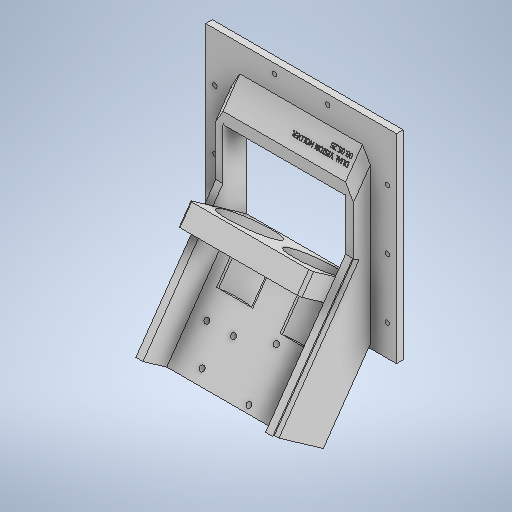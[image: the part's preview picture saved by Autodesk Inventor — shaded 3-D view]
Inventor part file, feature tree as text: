
AUTODESK INVENTOR PART (.ipt)
format: ipt  version: 2025.2 (Build 292293000, 293)  size: 1,523,200 bytes
history: native  units: in
note: dims shown in document units (in); Inventor stores cm internally (conversion verified against a paired STEP export)
features: sketch x51, extrude x46, projected_geometry x8, plane x5, chamfer x2, move_body x1, fillet x1, hole x1
ambient origin geometry x8: Origin, YZ Plane, XZ Plane, XY Plane, X Axis, Y Axis, Z Axis, Center Point
bodies: Solid1 (feature_tree)
feature tree (115):
  extrude  "Extrusion1"  Depth=0.1969in TaperAngle=0.0deg
  move_body  "Move Body1"
  plane  "Work Plane1"
  sketch  "Sketch5"  dims[d5=1.7717in d6=1.7717in d7=1.7717in d8=1.7717in d9=0.8108in d10=90.0deg d11=0.0787in d12=0.3701in d13=0.4252in d14=0.1362in d15=-0.0984in d16=-0.0591in d17=0.0in]
  plane  "Work Plane2"
  extrude  "Extrusion4"  TaperAngle=0.0deg  [1 undecoded]
  extrude  "Extrusion6"  Depth=0.2405in
  extrude  "Extrusion8"  Depth=2.5591in TaperAngle=0.0deg
  chamfer  "Chamfer1"  [1 undecoded]
  extrude  "Extrusion11"  Depth=0.2362in
  plane  "Work Plane3"
  extrude  "Extrusion13"  Depth=0.1969in TaperAngle=0.0deg
  plane  "Work Plane4"
  plane  "Work Plane6"
  extrude  "Extrusion21"  Depth=0.5027in
  extrude  "Extrusion22"  Depth=0.5027in
  extrude  "Extrusion25"  Depth=1.1811in TaperAngle=0.0deg
  extrude  "Extrusion26"  Depth=0.1969in
  sketch  "Sketch33"  dims[d100=3.6403in d101=2.7717in]
  extrude  "Extrusion27"  Depth=0.2362in TaperAngle=0.0deg
  extrude  "Extrusion29"  Depth=3.6403in
  extrude  "Extrusion28"  Depth=0.6299in TaperAngle=0.0deg
  sketch  "Sketch36"  dims[d124=0.9712in d125=0.0in d126=0.5906in d127=0.0in]
  extrude  "Extrusion30"  Depth=0.7874in
  extrude  "Extrusion31"  Depth=0.5906in TaperAngle=0.0deg
  sketch  "Sketch39"  dims[d164=0.1181in d165=0.0in d168=0.5906in d169=0.0in]
  extrude  "Extrusion35"  Depth=11.3469in TaperAngle=0.0deg
  sketch  "Sketch45"  dims[d176=0.7313in d177=0.0in d186=0.0in d187=0.0in]
  extrude  "Extrusion37"  Depth=0.1181in TaperAngle=0.0deg
  extrude  "Extrusion38"  Depth=0.1181in TaperAngle=0.0deg
  extrude  "Extrusion40"  TaperAngle=0.0deg  [1 undecoded]
  extrude  "Extrusion41"  TaperAngle=0.0deg  [1 undecoded]
  extrude  "Extrusion43"  TaperAngle=0.0deg  [1 undecoded]
  extrude  "Extrusion44"  Depth=0.0394in TaperAngle=0.0deg
  extrude  "Extrusion46"  Depth=3.9671in TaperAngle=0.0deg
  extrude  "Extrusion47"  Depth=0.1969in
  extrude  "Extrusion48"  TaperAngle=60.0deg  [1 undecoded]
  sketch  "Sketch61"  dims[d257=0.1181in d258=0.0in d259=0.0787in d260=0.0in]
  extrude  "Extrusion50"  Depth=0.1969in
  extrude  "Extrusion51"  Depth=0.3937in
  extrude  "Extrusion52"  Depth=0.3937in
  extrude  "Extrusion53"  Depth=0.0787in TaperAngle=0.0deg
  extrude  "Extrusion54"  Depth=0.3937in TaperAngle=0.0deg
  extrude  "Extrusion57"  TaperAngle=0.0deg  [1 undecoded]
  extrude  "Extrusion59"  Depth=0.8268in
  extrude  "Extrusion60"  TaperAngle=0.0deg  [1 undecoded]
  extrude  "Extrusion61"  Depth=1.1614in
  extrude  "Extrusion62"  Depth=0.6299in TaperAngle=0.0deg
  extrude  "Extrusion63"  Depth=0.1969in TaperAngle=0.0deg
  extrude  "Extrusion64"  Depth=0.1181in TaperAngle=0.0deg
  extrude  "Extrusion65"  Depth=0.1575in
  extrude  "Extrusion70"  Depth=0.9843in
  extrude  "Extrusion74"  Depth=1.4173in
  extrude  "Extrusion75"  Depth=3.6405in
  fillet  "Fillet2"  Radius=3.6405in
  extrude  "Extrusion76"  Depth=0.1772in
  extrude  "Extrusion77"  Depth=0.0787in
  extrude  "Extrusion78"  Depth=0.2756in
  extrude  "Extrusion81"  Depth=0.1181in
  chamfer  "Chamfer3"  Distance=0.1181in
  extrude  "Extrusion82"  Depth=0.0197in
  sketch  "Sketch1"  dims[d1=0.5512in d2=0.1969in d3=0.0in]
  sketch  "Sketch6"  dims[d18=0.2749in d24=0.2405in]
  sketch  "Sketch8"  dims[d25=2.7559in d26=0.0in d29=2.5591in d30=0.0in d36=0.0in d37=0.0in]
  sketch  "Sketch12"  dims[d42=0.2362in d43=0.2362in]
  sketch  "Sketch15"  dims[d52=0.2362in d53=0.0787in d54=45.0deg d55=0.1969in d56=0.0in]
  sketch  "Sketch17"  dims[d59=0.5906in d60=0.0in d76=0.5027in]
  sketch  "Sketch27"  dims[d77=0.5027in d78=0.5027in]
  sketch  "Sketch28"  dims[d79=0.5027in d81=1.1811in d82=0.0in]
  sketch  "Sketch31"  dims[d83=0.0in d84=0.0in d91=0.1969in]
  sketch  "Sketch32"  dims[d94=0.2362in d95=0.0in d96=0.2362in d97=0.0in]
  sketch  "Sketch34"  dims[d112=1.9685in d113=0.6299in d114=0.0in]
  sketch  "Sketch35"  dims[d115=0.1575in d117=0.1575in d122=0.7874in d123=0.9331in]
  sketch  "Sketch37"  dims[d128=11.3469in d129=0.0in d130=11.3469in d131=0.0in]
  sketch  "Sketch38"  dims[d141=0.6299in d156=0.1181in d157=0.0in]
  sketch  "Sketch44"  dims[d170=4.7244in d171=0.0in d174=0.0in d175=0.0in]
  projected_geometry  "Projected Loop2"
  projected_geometry  "Projected Loop3"
  projected_geometry  "Projected Loop5"
  sketch  "Sketch47"  dims[d188=0.0in d189=0.0in d194=0.0in d195=0.0in]
  sketch  "Sketch49"  dims[d198=0.0591in d199=0.0in d200=0.0394in d201=0.0in]
  sketch  "Sketch50"  dims[d235=6.1063in d236=0.0in d244=3.9671in d245=0.0in]
  sketch  "Sketch52"  dims[d246=0.9963in d248=0.1969in]
  sketch  "Sketch53"  dims[d249=0.1378in d250=60.0deg]
  sketch  "Sketch56"  dims[d251=0.1969in d252=0.1378in]
  sketch  "Sketch58"  dims[d253=60.0deg d254=0.3937in]
  sketch  "Sketch59"  dims[d255=0.3937in d256=0.3937in]
  sketch  "Sketch63"  dims[d261=1.9685in d262=0.0in d271=0.3937in d272=0.0in]
  sketch  "Sketch64"  dims[d275=0.3937in d276=0.0in d277=0.0in d278=0.0in]
  sketch  "Sketch65"  dims[d279=1.4567in d280=0.8268in]
  sketch  "Sketch66"  dims[d281=1.2598in d282=0.0in d283=0.0in]
  sketch  "Sketch67"  dims[d284=1.5748in d287=1.1614in]
  sketch  "Sketch70"  dims[d288=0.8512in d289=0.6299in d290=0.0in]
  sketch  "Sketch72"  dims[d291=2.9921in d292=0.0in d293=0.1969in d294=0.0in]
  sketch  "Sketch75"  dims[d295=0.1181in d296=0.0in d314=0.0197in d315=0.0in]
  sketch  "Sketch76"  dims[d331=0.315in d332=0.1575in]
  sketch  "Sketch77"  dims[d333=0.1575in d334=0.9843in]
  sketch  "Sketch79"  dims[d335=0.1575in d336=1.4173in]
  projected_geometry  "Projected Loop11"
  sketch  "Sketch80"  dims[d337=0.1575in d338=0.9843in d339=3.6405in d340=0.0in]
  projected_geometry  "Projected Loop12"
  sketch  "Sketch81"  dims[d341=1.4173in d342=0.1772in]
  sketch  "Sketch86"  dims[d343=0.9843in d344=0.0in d346=0.0787in]
  projected_geometry  "Projected Loop14"
  sketch  "Sketch90"  dims[d347=0.2756in d348=0.2756in]
  sketch  "Sketch92"  dims[d349=0.2756in d351=0.2756in d352=0.1181in d353=0.0in]
  sketch  "Sketch94"  dims[d354=0.1956in d355=0.0in d356=0.0197in]
  sketch  "Sketch95"  dims[d357=0.0in d358=0.0in d363=3.6403in d364=0.0in]
  projected_geometry  "Projected Loop15"
  projected_geometry  "Projected Loop16"
  sketch  "Sketch96"  dims[d365=0.0787in d366=0.0787in d367=45.0deg]
  sketch  "Sketch99"  dims[d371=0.3543in]
  sketch  "Sketch100"  dims[d372=0.3543in d373=0.3543in d374=0.3543in d375=0.1181in d376=0.1181in d377=0.0984in d378=0.0in d38=0.0197in d39=0.0344in d57=0.0197in d58=0.0344in d158=0.0197in d159=0.0344in d178=0.0in d179=0.0in d180=0.0in d181=0.0in d202=0.0197in d203=0.0344in d359=0.0344in]
  sketch  "Sketch2"  dims[d4=0.315in]
  hole  "Hole1"  [1 undecoded]
note: 9 required parameter values undecoded (feature->parameter linkage not recoverable at this tier; creation-order binding heuristic only, values carry confidence <= 0.55)
